# Revit family: NBS_BetafenceLimited_MtlMeshPnlFncngSym_RollTop-Twilfix
name_source: partatom
category: Site
revit_build: Autodesk Revit 2017 (Build: 20171027_0315(x64)
units: mm (PartAtom-declared; Revit-internal decimal feet)

## family parameters
Cut with Voids When Loaded = No
Part Type = Normal
Round Connector Dimension = Use Diameter
Shared = No

## types (1)
- Roll Top + Twilfix
    Applications = School, sport, parks and playgrounds, company premises
    AssetType = Fixed
    BIMObjectName = NBS_BetafenceLimited_MetalMeshPanelFencingSystem_RollTop-Twilfix
    Category = Ss_25_14_67_51: Metal mesh panel fencing systems
    Color = Green (RAL 6005)
    Description = Perimeter security
    Diameter = 0 mm  [stored 0 ft]
    DurationUnit = year
    Finish = Polyester coating
    FoundationMaterial = NBS_Concept
    Gradient01Maximum = 3.33%
    Gradient01PostAxisDistance = 3000 mm  [stored 9.84252 ft]
    Gradient02Maximum = 4.00%
    Gradient02PostAxisDistance = 2500 mm
    Gradient03Maximum = 5.00%
    Gradient03PostAxisDistance = 2000 mm  [stored 6.56168 ft]
    Gradient04Maximum = 6.67%
    Gradient04PostAxisDistance = 1500 mm
    GradientMaximumPostAxisDistance = 1000 mm  [stored 3.28084 ft]
    Height = 2400 mm
    IfcExportAs = IfcWallType
    IfcExportType = NOTDEFINED
    IsExternal = Yes
    ManufacturerName = Betafence Limited
    ManufacturerURL = www.betafence.co.uk
    Material = hot-dip zinc coated steel sheet (Sendzimir) and afterwards polyester coated
    MaximumIncline = 10.00%
    ModelReference = Roll Top + Twilfix
    NBSCertification = www.nationalbimlibrary.com/cert/nlyi0i25
    NBSDescription = Metal mesh panel fencing system
    NBSReference = 25-20-30/145
    Name = MetalMeshPanelFencingSystem_RollTop+Twilfix_BetafenceLimited
    NominalHeight = 2400 mm
    NominalLength = 0 mm  [stored 0 ft]
    NominalWidth = 3025 mm
    PanelElevationAboveFoundation = 270 mm  [stored 0.885827 ft]
    PanelHeight = 2400 mm
    PanelMaterial = NBS_BetafenceLimited_MtlMeshPnlFncngSym_RollTop_Panel
    PanelOffsetFromPost = 10 mm  [stored 0.0328084 ft]
    PanelOffsetFromPostCL = 75 mm  [stored 0.246063 ft]
    PanelSizeOptions = 3000 x 900 mm, 3000 x 1200 mm, 3000 x 1500 mm, 3000 x 1800 mm, 3000 x (2 x 1200 mm)
    PanelThickness = 45 mm  [stored 0.147638 ft]
    PostHeightAboveGround = 2470 mm  [stored 8.10367 ft]
    PostHeightBelowGround = 200 mm  [stored 0.656168 ft]
    PostMaterial = NBS_Concept
    PostThickness = 60 mm  [stored 0.19685 ft]
    PostWidth = 60 mm  [stored 0.19685 ft]
    Posts = Twilfix
    ProductInformation = www.betafence.co.uk/en/roll-top
    SecurityLevel = General purpose and security
    StandardPostAxisDistance = 3025 mm
    Uniclass2015Code = Ss_25_14_67_51
    Uniclass2015Title = Metal mesh panel fencing systems
    Uniclass2015Version = Systems v1.13
    Version = 2
    WarrantyDurationUnit = year

note: [stored X ft] marks values corroborated as IEEE doubles in the binary element streams (Revit-internal decimal feet)

## geometry (parser evidence)
native form markers: Sweep x8
no freeform markers — native parametric forms only
